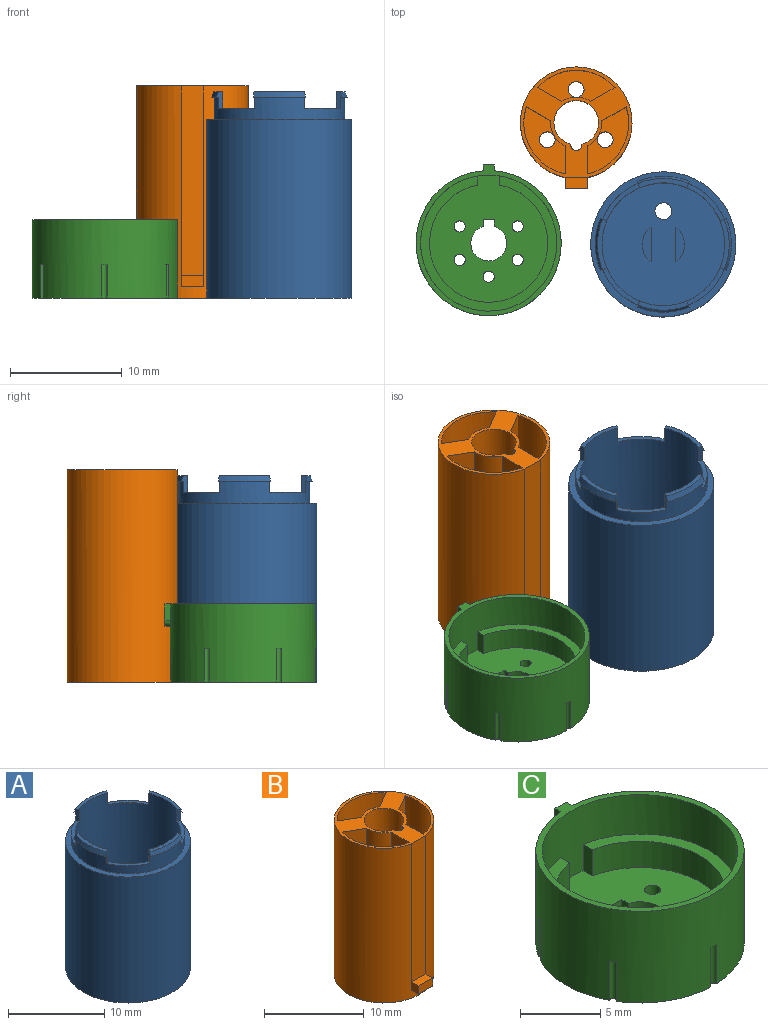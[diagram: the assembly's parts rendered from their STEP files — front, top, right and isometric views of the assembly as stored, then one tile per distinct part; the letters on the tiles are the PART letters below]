
ASSEMBLY  parts=3 mates=2
PART A: 37 faces, bbox 13x13x18.5 mm
  f0: cylinder r=1.9mm len=3.1mm, axis (0,0,-1), area 10.9mm2, adj f11,f34,f35
  f1: cylinder r=1.9mm len=3.1mm, axis (0,0,-1), area 10.9mm2, adj f2,f11,f36
  f2: plane 3.1x0.8mm, normal (0,0,1), area 1.7mm2, adj f1,f36
  f3: plane 3.35x3.35mm, normal (0,0,1), area 1.8mm2, adj f10,f12,f20,f22
  f4: plane 3.35x3.35mm, normal (0,0,1), area 1.8mm2, adj f10,f12,f17,f19
  f5: plane 3.35x3.35mm, normal (0,0,1), area 1.8mm2, adj f10,f12,f14,f16
  f6: plane 3.35x3.35mm, normal (0,0,1), area 1.8mm2, adj f10,f12,f13,f23
  f7: cylinder r=6.5mm len=16mm, axis (0,0,-1), area 653.5mm2, adj f8,f9
  f8: plane 13x13mm, normal (0,0,1), area 23.4mm2, adj f7,f10
  f9: plane 13x13mm, normal (0,0,-1), area 131mm2, adj f7,f33
  f10: cylinder r=5.9mm len=11.8mm, axis (0,0,-1), area 55.6mm2, adj f3,f4,f5,f6,f8,f13,f14,f16
  f11: plane 11x11mm, normal (0,0,1), area 89.8mm2, adj f0,f1,f12,f33,f35,f36
  f12: cylinder r=5.5mm len=17.5mm, axis (0,0,-1), area 578.8mm2, adj f3,f4,f5,f6,f11,f13,f14,f15
  f13: plane 1.5x0.55mm, normal (0.92,-0.38,0), area 0.7mm2, adj f6,f10,f12,f15,f25,f26
  f14: plane 1.5x0.55mm, normal (-0.92,-0.38,0), area 0.7mm2, adj f5,f10,f12,f15,f25,f26
  f15: plane 4.52x0.82mm, normal (0,0,1), area 1.8mm2, adj f12,f13,f14,f25
  f16: plane 1.5x0.55mm, normal (0.38,0.92,0), area 0.7mm2, adj f5,f10,f12,f18,f27,f28
  f17: plane 1.5x0.55mm, normal (0.38,-0.92,0), area 0.7mm2, adj f4,f10,f12,f18,f27,f28
  f18: plane 4.52x0.82mm, normal (0,0,1), area 1.8mm2, adj f12,f16,f17,f27
  f19: plane 1.5x0.55mm, normal (-0.92,0.38,0), area 0.7mm2, adj f4,f10,f12,f21,f29,f30
  f20: plane 1.5x0.55mm, normal (0.92,0.38,0), area 0.7mm2, adj f3,f10,f12,f21,f29,f30
  f21: plane 4.52x0.82mm, normal (0,0,1), area 1.8mm2, adj f12,f19,f20,f29
  f22: plane 1.5x0.55mm, normal (-0.38,-0.92,0), area 0.7mm2, adj f3,f10,f12,f24,f31,f32
  f23: plane 1.5x0.55mm, normal (-0.38,0.92,0), area 0.7mm2, adj f6,f10,f12,f24,f31,f32
  f24: plane 4.52x0.82mm, normal (0,0,1), area 1.8mm2, adj f12,f22,f23,f31
  f25: cone r=5.9mm half-angle=21.8deg, axis (0,0,-1), area 2.5mm2, adj f13,f14,f15,f26
  f26: plane 4.67x0.65mm, normal (0,0,-1), area 0.9mm2, adj f10,f13,f14,f25
  f27: cone r=5.9mm half-angle=21.8deg, axis (0,0,-1), area 2.5mm2, adj f16,f17,f18,f28
  f28: plane 4.67x0.65mm, normal (0,0,-1), area 0.9mm2, adj f10,f16,f17,f27
  f29: cone r=5.9mm half-angle=21.8deg, axis (0,0,-1), area 2.5mm2, adj f19,f20,f21,f30
  f30: plane 4.67x0.65mm, normal (0,0,-1), area 0.9mm2, adj f10,f19,f20,f29
  f31: cone r=5.9mm half-angle=21.8deg, axis (0,0,-1), area 2.5mm2, adj f22,f23,f24,f32
  f32: plane 4.67x0.65mm, normal (0,0,-1), area 0.9mm2, adj f10,f22,f23,f31
  f33: cylinder r=0.75mm len=1.5mm, axis (0,0,1), area 4.7mm2, adj f9,f11
  f34: plane 3.1x0.8mm, normal (0,0,1), area 1.7mm2, adj f0,f35
  f35: plane 3.1x3mm, normal (-1,0,0), area 9.3mm2, adj f0,f11,f34
  f36: plane 3.1x3mm, normal (1,0,0), area 9.3mm2, adj f1,f2,f11
PART B: 29 faces, bbox 10x10.9x19 mm
  f0: plane 17x2mm, normal (0,-1,0), area 34mm2, adj f1,f2,f24
  f1: plane 10x9.9mm, normal (0,0,1), area 27.3mm2, adj f0,f2,f4,f5,f6,f7,f8,f9
  f2: cylinder r=5mm len=19mm, axis (0,0,-1), area 560.7mm2, adj f0,f1,f3,f25,f26,f27
  f3: plane 10x10mm, normal (0,0,-1), area 60.9mm2, adj f2,f4,f5,f21,f22,f23
  f4: cylinder r=0.5mm len=19mm, axis (0,0,1), area 32.2mm2, adj f1,f3,f5
  f5: cylinder r=2mm len=19mm, axis (0,0,1), area 219.7mm2, adj f1,f3,f4
  f6: cylinder r=2.3mm len=14mm, axis (0,0,1), area 38.5mm2, adj f1,f7,f9,f10
  f7: plane 14x2.52mm, normal (1,0,0), area 35.3mm2, adj f1,f6,f8,f10
  f8: cylinder r=4.7mm len=14mm, axis (0,0,1), area 109.6mm2, adj f1,f7,f9,f10
  f9: plane 14x2.18mm, normal (0.5,-0.87,0), area 35.3mm2, adj f1,f6,f8,f10
  f10: plane 6.02x3.7mm, normal (0,0,1), area 11.2mm2, adj f6,f7,f8,f9,f23
  f11: cylinder r=2.3mm len=14mm, axis (0,0,1), area 38.5mm2, adj f1,f12,f14,f15
  f12: plane 14x2.18mm, normal (-0.5,-0.87,0), area 35.3mm2, adj f1,f11,f13,f15
  f13: cylinder r=4.7mm len=14mm, axis (0,0,1), area 109.6mm2, adj f1,f12,f14,f15
  f14: plane 14x2.52mm, normal (-1,0,0), area 35.3mm2, adj f1,f11,f13,f15
  f15: plane 6.02x3.7mm, normal (0,0,1), area 11.2mm2, adj f11,f12,f13,f14,f22
  f16: cylinder r=2.3mm len=14mm, axis (0,0,1), area 38.5mm2, adj f1,f17,f19,f20
  f17: plane 14x2.18mm, normal (-0.5,0.87,0), area 35.3mm2, adj f1,f16,f18,f20
  f18: cylinder r=4.7mm len=14mm, axis (0,0,1), area 109.6mm2, adj f1,f17,f19,f20
  f19: plane 14x2.18mm, normal (0.5,0.87,0), area 35.3mm2, adj f1,f16,f18,f20
  f20: plane 6.95x2.8mm, normal (0,0,1), area 11.2mm2, adj f16,f17,f18,f19,f21
  f21: cylinder r=0.7mm len=5mm, axis (0,0,-1), area 22mm2, adj f3,f20
  f22: cylinder r=0.7mm len=5mm, axis (0,0,-1), area 22mm2, adj f3,f15
  f23: cylinder r=0.7mm len=5mm, axis (0,0,-1), area 22mm2, adj f3,f10
  f24: plane 2x1mm, normal (0,0,1), area 2mm2, adj f0,f25,f27,f28
  f25: plane 1x1mm, normal (-1,0,0), area 1mm2, adj f2,f24,f26,f28
  f26: plane 2x1mm, normal (0,0,-1), area 1.9mm2, adj f2,f25,f27,f28
  f27: plane 1x1mm, normal (1,0,0), area 1mm2, adj f2,f24,f26,f28
  f28: plane 2x1mm, normal (0,-1,0), area 2mm2, adj f24,f25,f26,f27
PART C: 34 faces, bbox 13x13.5x7 mm
  f0: plane 13x12.99mm, normal (0,0,-1), area 119.7mm2, adj f1,f9,f10,f11,f12,f13,f14,f15
  f1: cylinder r=6.5mm len=13mm, axis (0,0,-1), area 275mm2, adj f0,f2,f18,f20,f21,f22,f23,f24
  f2: plane 13.5x13mm, normal (0,0,1), area 16.3mm2, adj f1,f3,f18,f19,f20
  f3: cylinder r=6.1mm len=12.2mm, axis (0,0,1), area 119mm2, adj f2,f4,f6,f7,f8
  f4: plane 12.2x12.12mm, normal (0,0,1), area 27mm2, adj f3,f5,f6,f7
  f5: cylinder r=5.3mm len=10.6mm, axis (0,0,1), area 62.6mm2, adj f4,f6,f7,f8
  f6: plane 2x0.81mm, normal (-1,0,0), area 1.6mm2, adj f3,f4,f5,f8
  f7: plane 2x0.81mm, normal (1,0,0), area 1.6mm2, adj f3,f4,f5,f8
  f8: plane 11.4x10.6mm, normal (0,0,1), area 77.4mm2, adj f3,f5,f6,f7,f9,f10,f11,f12
  f9: plane 2x0.58mm, normal (-1,0,0), area 1.2mm2, adj f0,f8,f10,f11
  f10: cylinder r=1.6mm len=3.2mm, axis (0,0,1), area 18.1mm2, adj f0,f8,f9,f12
  f11: plane 2x1mm, normal (0,-1,0), area 2mm2, adj f0,f8,f9,f12
  f12: plane 2x0.58mm, normal (1,0,0), area 1.2mm2, adj f0,f8,f10,f11
  f13: cylinder r=0.5mm len=2mm, axis (0,0,1), area 6.3mm2, adj f0,f8
  f14: cylinder r=0.5mm len=2mm, axis (0,0,1), area 6.3mm2, adj f0,f8
  f15: cylinder r=0.5mm len=2mm, axis (0,0,1), area 6.3mm2, adj f0,f8
  f16: cylinder r=0.5mm len=2mm, axis (0,0,1), area 6.3mm2, adj f0,f8
  f17: cylinder r=0.5mm len=2mm, axis (0,0,1), area 6.3mm2, adj f0,f8
  f18: plane 1.5x0.52mm, normal (1,0,0), area 0.8mm2, adj f1,f2,f19,f21
  f19: plane 2x1mm, normal (0,1,0), area 1.9mm2, adj f2,f18,f20,f21
  f20: plane 1.5x0.52mm, normal (-1,0,0), area 0.8mm2, adj f1,f2,f19,f21
  f21: cylinder r=0.5mm len=1mm, axis (0,1,0), area 0.8mm2, adj f1,f18,f19,f20
  f22: plane 0.46x0.37mm, normal (0,0,-1), area 0.1mm2, adj f1,f23
  f23: cylinder r=0.25mm len=3mm, axis (0,0,-1), area 2.3mm2, adj f0,f1,f22
  f24: plane 0.46x0.37mm, normal (0,0,-1), area 0.1mm2, adj f1,f25
  f25: cylinder r=0.25mm len=3mm, axis (0,0,-1), area 2.3mm2, adj f0,f1,f24
  f26: plane 0.5x0.25mm, normal (0,0,-1), area 0.1mm2, adj f1,f27
  f27: cylinder r=0.25mm len=3mm, axis (0,0,-1), area 2.3mm2, adj f0,f1,f26
  f28: plane 0.46x0.37mm, normal (0,0,-1), area 0.1mm2, adj f1,f29
  f29: cylinder r=0.25mm len=3mm, axis (0,0,-1), area 2.3mm2, adj f0,f1,f28
  f30: plane 0.46x0.37mm, normal (0,0,-1), area 0.1mm2, adj f1,f31
  f31: cylinder r=0.25mm len=3mm, axis (0,0,-1), area 2.3mm2, adj f0,f1,f30
  f32: plane 0.5x0.25mm, normal (0,0,-1), area 0.1mm2, adj f1,f33
  f33: cylinder r=0.25mm len=3mm, axis (0,0,-1), area 2.3mm2, adj f0,f1,f32
PLACE A t=(7.81,-3.17,-14.36)mm
PLACE B t=(0.01,7.73,-14.36)mm
PLACE C t=(-7.84,-3.04,-14.36)mm
MATE planar B.f2 <-> C.f0  axis (0,0,-1) through (0.01,7.73,-14.36)mm
MATE planar C.f14 <-> A.f7  axis (0,0,-1) through (-10.43,-1.54,-14.36)mm
